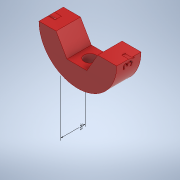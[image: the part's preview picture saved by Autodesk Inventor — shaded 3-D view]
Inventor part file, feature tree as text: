
AUTODESK INVENTOR PART (.ipt)
format: ipt  version: 2022.1 (Build 261234000, 234)  size: 838,144 bytes
history: native  units: in
note: dims shown in document units (in); Inventor stores cm internally (conversion verified against a paired STEP export)
features: sketch x4, other x2, extrude x2, thicken_offset x1, plane x1, emboss x1, hole x1, split x1
ambient origin geometry x8: Origin, YZ Plane, XZ Plane, XY Plane, X Axis, Y Axis, Z Axis, Center Point
bodies: Solid1 (feature_tree)
feature tree (13):
  other  "Annotations"
  extrude  "Extrusion1"  Depth=1.125in
  thicken_offset  "Thicken2"
  plane  "Work Plane1"
  emboss  "Emboss1"
  hole  "Hole1"  [1 undecoded]
  extrude  "Extrusion2"  Depth=0.0225in
  split  "Split1"
  sketch  "Sketch1"  dims[d0=0.5in d2=1.125in]
  sketch  "Sketch2"  dims[d3=0.2738in d4=0.375in d5=0.0in]
  sketch  "Sketch3"  dims[d8=0.0225in d9=0.0225in]
  sketch  "Sketch4"  dims[d17=1.0in d18=0.25in d19=0.1in d20=0.0in d21=0.17in d22=0.75in d23=0.5in d24=0.093in d25=0.5635in d26=1.0in d27=0.8108in d28=0.1763in d29=0.1763in d30=0.191in d31=0.2186in d32=0.0in d14=0.1112in d15=0.3058in d16=0.3525in]
  other  "Linear Dimension 2"
note: 1 required parameter value undecoded (feature->parameter linkage not recoverable at this tier; creation-order binding heuristic only, values carry confidence <= 0.55)
